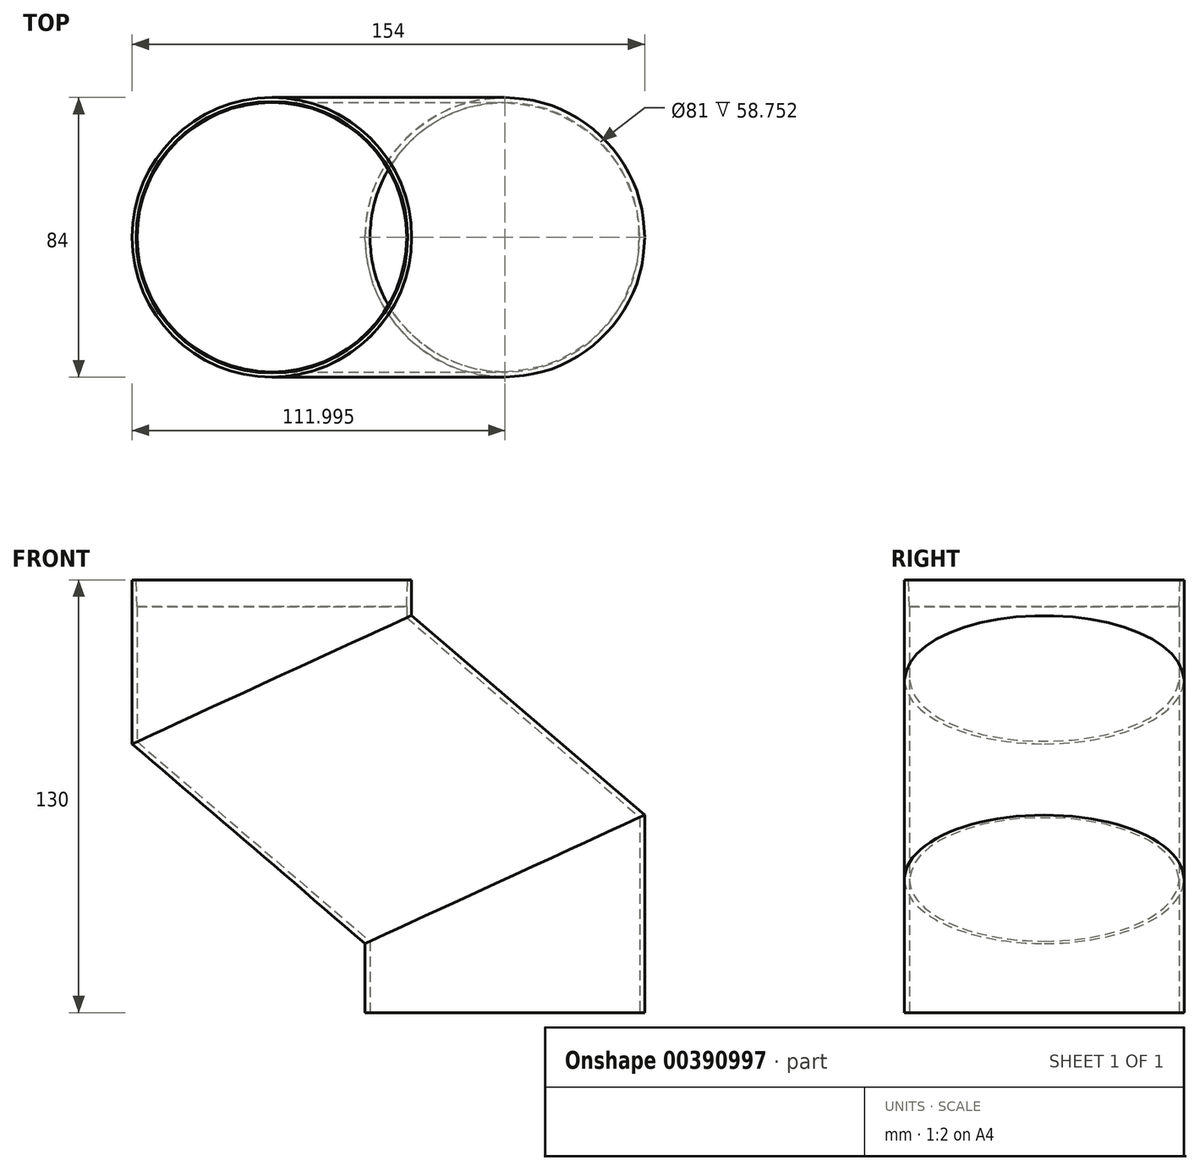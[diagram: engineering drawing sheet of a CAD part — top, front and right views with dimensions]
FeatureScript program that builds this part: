
annotation { "Feature Type Name" : "Feature", "Feature Type Description" : "" }
export const myFeature = defineFeature(function(context is Context, id is Id, definition is map)
    precondition{}
    {
        {
            var Q0;
            Q0=qCreatedBy(makeId("Front.planeOp"),FACE);
            var sketch = newSketch(context, id + "F0", { "sketchPlane" : qUnion([Q0])});
            skLineSegment(sketch, "E0", {"start": v(0, 0) * mm, "end": v(0, -30) * mm});
            skLineSegment(sketch, "E1", {"start": v(0, -30) * mm, "end": v(70, -90) * mm});
            skLineSegment(sketch, "E2", {"start": v(70, -90) * mm, "end": v(70, -130) * mm});
            skSolve(sketch);
        }
        {
            var Q0;
            Q0=qCreatedBy(makeId("Top.planeOp"),FACE);
            var sketch = newSketch(context, id + "F1", { "sketchPlane" : qUnion([Q0])});
            skCircle(sketch, "E3", {"center": v(0.14, -0.24) * mm, "radius": 42 * mm});
            skSolve(sketch);
        }
        {
            var Q0;
            Q0=makeQuery(id+"F1.imprint","IMPRINT",FACE,{"disambiguationData":[TD([[makeQuery(id+"F1.imprint","IMPRINT",EDGE,{"derivedFrom":sQuery(id+"F1.wireOp",EDGE,"E3")}),1.0]])]});
            var Q1;
            Q1=sQuery(id+"F0.wireOp",EDGE,"E0");
            var Q2;
            Q2=sQuery(id+"F0.wireOp",EDGE,"E1");
            var Q3;
            Q3=sQuery(id+"F0.wireOp",EDGE,"E2");
            sweep(context, id + "F2", {"profiles" : qUnion([Q0]), "path" : qUnion([Q1, Q2, Q3])});
        }
        {
            var Q0;
            Q0=makeQuery(id+"F2.opSweep","CAP_FACE",FACE,{"disambiguationData":[OSD([sQuery(id+"F0.wireOp",VERTEX,"E0.start"),sQuery(id+"F1.wireOp",EDGE,"E3")])],"isStart":true});
            shell(context, id + "F3", {"entities" : qUnion([Q0]), "thickness" : 1.5 * mm});
        }
        {
            var Q0;
            Q0=makeQuery(id+"F2.opSweep","CAP_FACE",FACE,{"disambiguationData":[OSD([sQuery(id+"F0.wireOp",VERTEX,"E2.end"),sQuery(id+"F1.wireOp",EDGE,"E3")])],"isStart":false});
            var sketch = newSketch(context, id + "F4", { "sketchPlane" : qUnion([Q0])});
            skPoint(sketch, "E4", {"position": v(70.14, 0.24) * mm});
            skSolve(sketch);
        }
        {
            var Q0;
            Q0=sQuery(id+"F4.wireOp",VERTEX,"E4");
            var Q1;
            Q1=makeQuery(id+"F2.opSweep","SWEPT_BODY",BODY,{"disambiguationData":[OSD([sQuery(id+"F0.wireOp",EDGE,"E2"),sQuery(id+"F1.wireOp",EDGE,"E3")])]});
            hole(context, id + "F5", {"style" : HoleStyle.SIMPLE, "endStyle" : HoleEndStyle.BLIND, "holeDiameter" : 81 * mm, "holeDepth" : 12 * mm, "isTappedThrough" : true, "tappedDepth" : 12 * mm, "tapClearance" : 3, "locations" : qUnion([Q0]), "scope" : qUnion([Q1])});
        }
        {
            var Q0;
            Q0=makeQuery(id+"F3.opShell","OFFSET_EDGE",EDGE,{"disambiguationData":[OSD([sQuery(id+"F0.wireOp",VERTEX,"E0.start"),sQuery(id+"F1.wireOp",EDGE,"E3")])]});
            chamfer(context, id + "F6", {"entities" : qUnion([Q0]), "chamferType" : ChamferType.TWO_OFFSETS, "width1" : 0.3 * mm, "oppositeDirection" : false, "width2" : 8 * mm, "tangentPropagation" : true});
        }
    });
